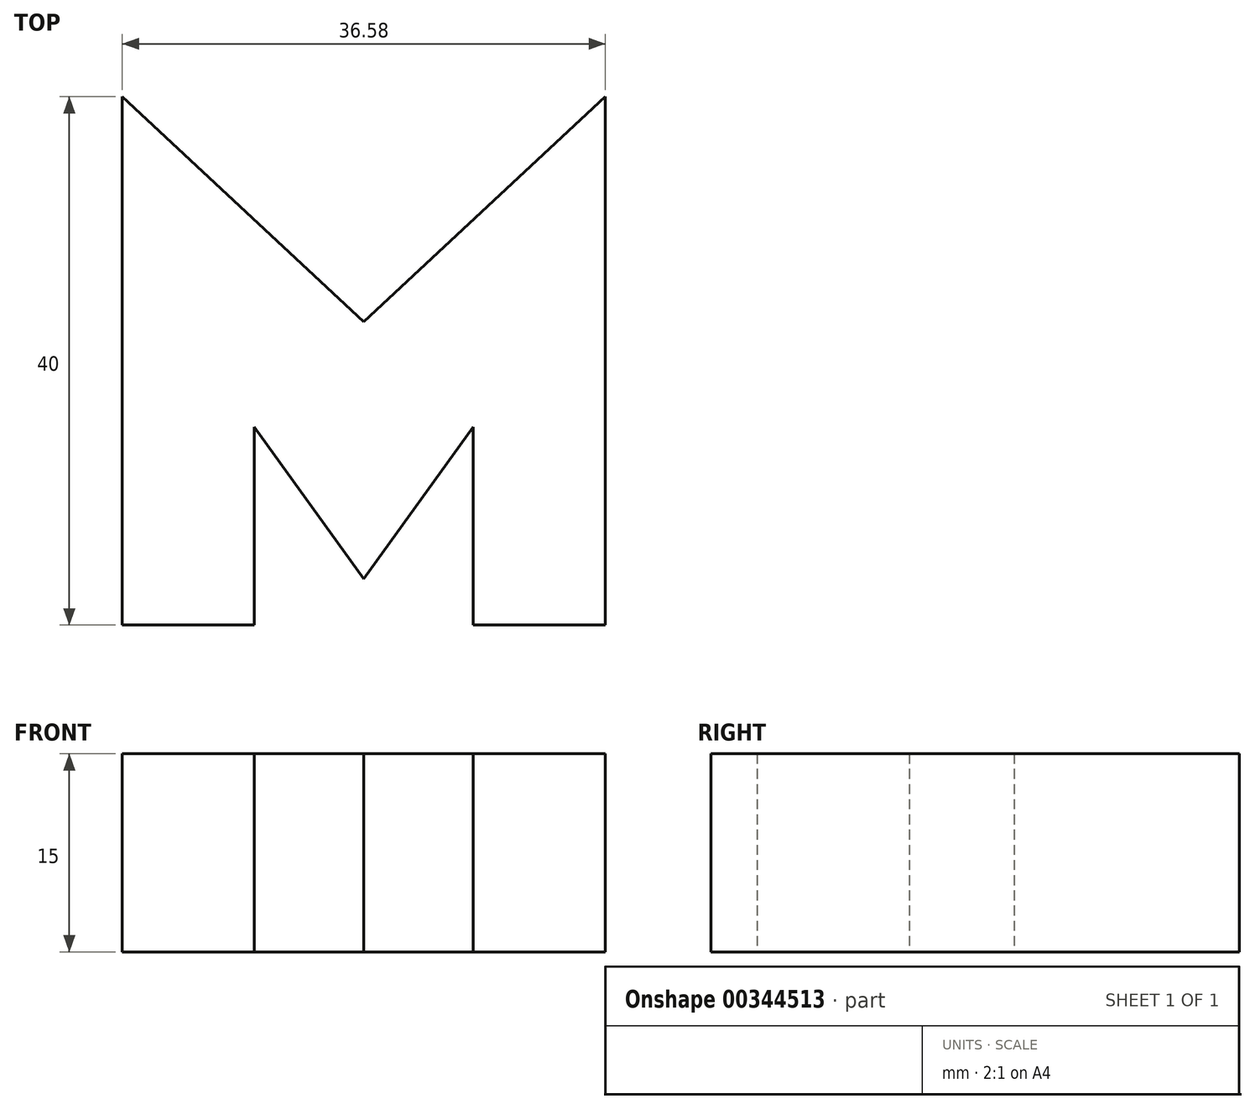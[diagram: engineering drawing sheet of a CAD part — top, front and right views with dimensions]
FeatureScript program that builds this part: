
annotation { "Feature Type Name" : "Feature", "Feature Type Description" : "" }
export const myFeature = defineFeature(function(context is Context, id is Id, definition is map)
    precondition{}
    {
        {
            var Q0;
            Q0=qCreatedBy(makeId("Top.planeOp"),FACE);
            var sketch = newSketch(context, id + "F0", { "sketchPlane" : qUnion([Q0])});
            skLineSegment(sketch, "E0", {"start": v(-36.58, 0) * mm, "end": v(-36.58, 40) * mm});
            skLineSegment(sketch, "E1", {"start": v(0, 0) * mm, "end": v(0, 40) * mm});
            skLineSegment(sketch, "E2", {"start": v(-36.58, 40) * mm, "end": v(-18.3, 22.96) * mm});
            skLineSegment(sketch, "E3", {"start": v(0, 40) * mm, "end": v(-18.3, 22.96) * mm});
            skLineSegment(sketch, "E4", {"start": v(-36.58, 0) * mm, "end": v(-26.58, 0) * mm});
            skLineSegment(sketch, "E5", {"start": v(0, 0) * mm, "end": v(-10, 0) * mm});
            skLineSegment(sketch, "E6", {"start": v(-10, 0) * mm, "end": v(-10, 15) * mm});
            skLineSegment(sketch, "E7", {"start": v(-26.58, 0) * mm, "end": v(-26.58, 15) * mm});
            skLineSegment(sketch, "E8", {"start": v(-26.58, 15) * mm, "end": v(-18.3, 3.49) * mm});
            skLineSegment(sketch, "E9", {"start": v(-10, 15) * mm, "end": v(-18.3, 3.49) * mm});
            skSolve(sketch);
        }
        {
            var Q0;
            Q0 = qSketchRegion(id + "F0", true);
            extrude(context, id + "F1", {"entities" : qUnion([Q0]), "depth" : 15 * mm});
        }
    });
